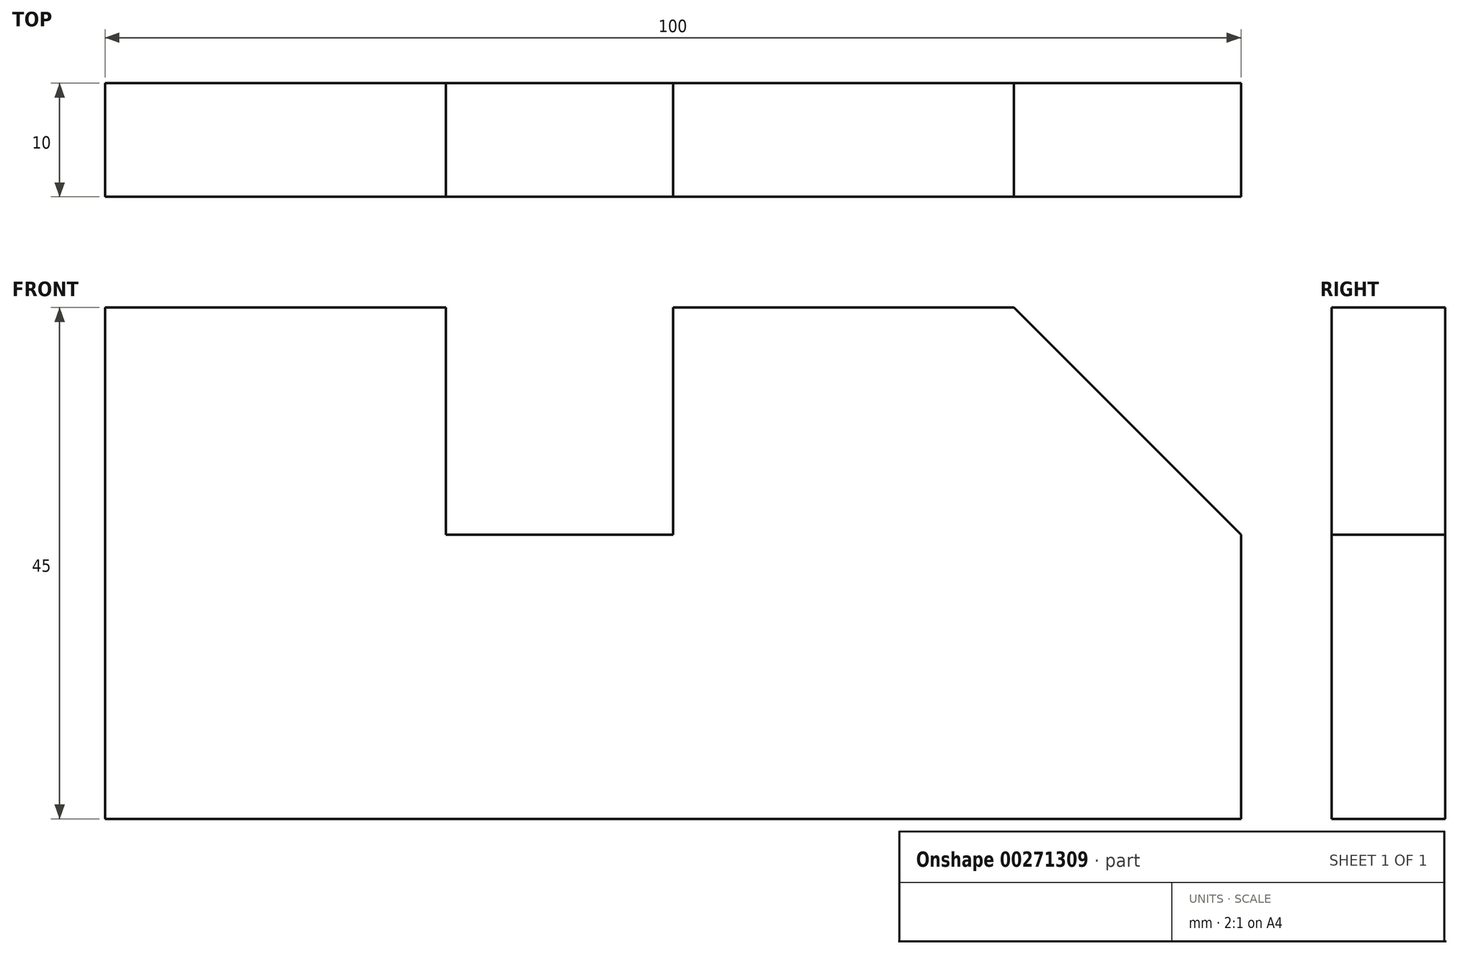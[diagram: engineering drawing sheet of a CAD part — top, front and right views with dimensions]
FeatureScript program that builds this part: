
annotation { "Feature Type Name" : "Feature", "Feature Type Description" : "" }
export const myFeature = defineFeature(function(context is Context, id is Id, definition is map)
    precondition{}
    {
        {
            var Q0;
            Q0=qCreatedBy(makeId("Front.planeOp"),FACE);
            var sketch = newSketch(context, id + "F0", { "sketchPlane" : qUnion([Q0])});
            skLineSegment(sketch, "E0", {"start": v(0, 0) * mm, "end": v(0, 45) * mm});
            skLineSegment(sketch, "E1", {"start": v(0, 45) * mm, "end": v(0, 45) * mm});
            skLineSegment(sketch, "E2", {"start": v(0, 45) * mm, "end": v(30, 45) * mm});
            skLineSegment(sketch, "E3", {"start": v(30, 45) * mm, "end": v(30, 25) * mm});
            skLineSegment(sketch, "E4", {"start": v(30, 25) * mm, "end": v(50, 25) * mm});
            skLineSegment(sketch, "E5", {"start": v(50, 25) * mm, "end": v(50, 45) * mm});
            skLineSegment(sketch, "E6", {"start": v(50, 45) * mm, "end": v(80, 45) * mm});
            skLineSegment(sketch, "E7", {"start": v(80, 45) * mm, "end": v(100, 25) * mm});
            skLineSegment(sketch, "E8", {"start": v(100, 25) * mm, "end": v(100, 0) * mm});
            skLineSegment(sketch, "E9", {"start": v(100, 0) * mm, "end": v(0, 0) * mm});
            skSolve(sketch);
        }
        {
            var Q0;
            Q0 = qSketchRegion(id + "F0", true);
            extrude(context, id + "F1", {"entities" : qUnion([Q0]), "depth" : 10 * mm});
        }
    });
